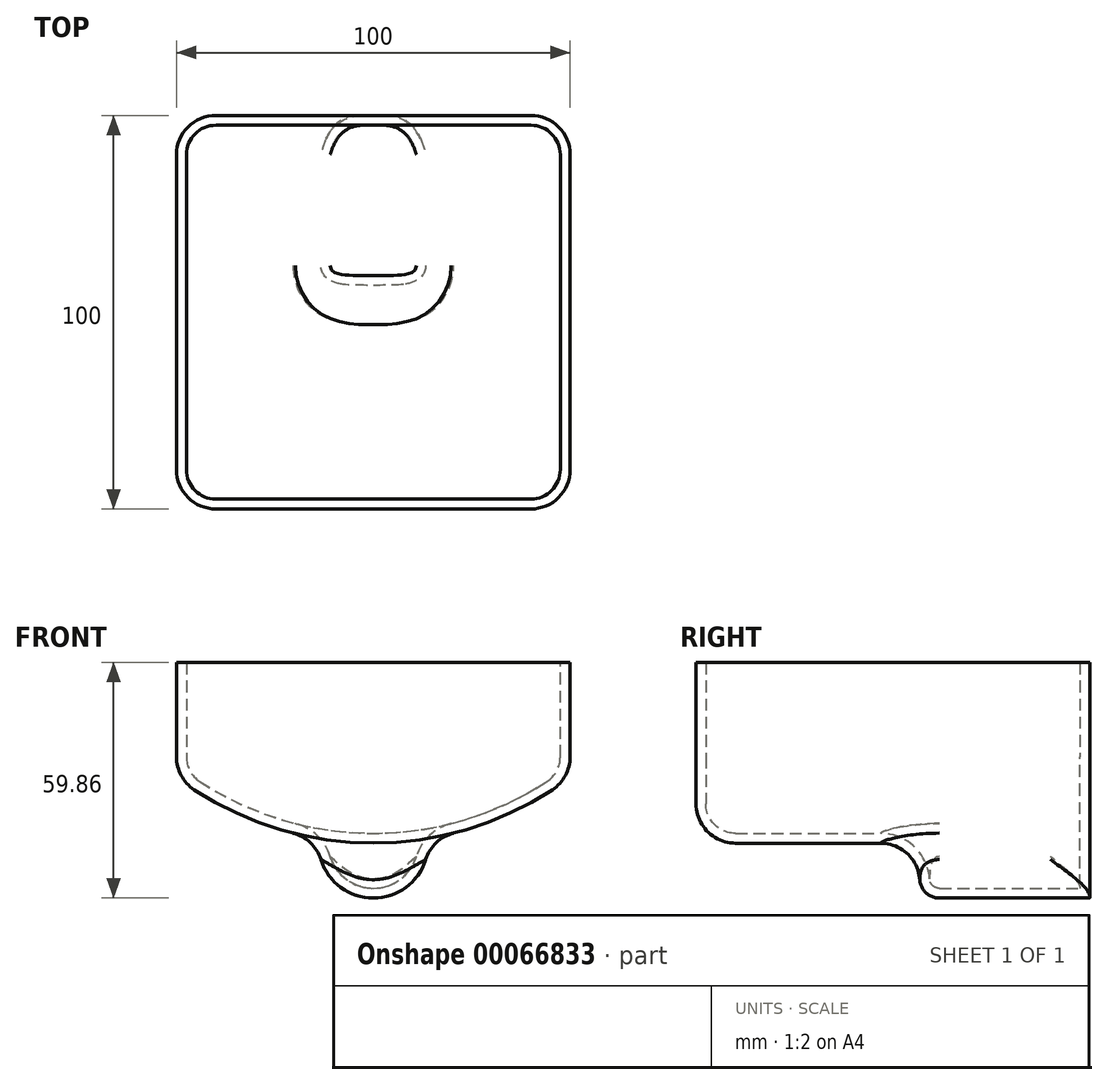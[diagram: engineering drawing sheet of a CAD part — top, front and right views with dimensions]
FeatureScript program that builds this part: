
annotation { "Feature Type Name" : "Feature", "Feature Type Description" : "" }
export const myFeature = defineFeature(function(context is Context, id is Id, definition is map)
    precondition{}
    {
        {
            var Q0;
            Q0=qCreatedBy(makeId("Top.planeOp"),FACE);
            var sketch = newSketch(context, id + "F0", { "sketchPlane" : qUnion([Q0])});
            skLineSegment(sketch, "E0.bottom", {"start": v(-60, -47.01) * mm, "end": v(40, -47.01) * mm});
            skLineSegment(sketch, "E0.top", {"start": v(-60, 52.99) * mm, "end": v(40, 52.99) * mm});
            skLineSegment(sketch, "E0.left", {"start": v(-60, -47.01) * mm, "end": v(-60, 52.99) * mm});
            skLineSegment(sketch, "E0.right", {"start": v(40, -47.01) * mm, "end": v(40, 52.99) * mm});
            skSolve(sketch);
        }
        {
            var Q0;
            Q0=makeQuery(id+"F0.imprint","IMPRINT",FACE,{"disambiguationData":[TD([[makeQuery(id+"F0.imprint","IMPRINT",EDGE,{"derivedFrom":sQuery(id+"F0.wireOp",EDGE,"E0.bottom")}),1.0]])]});
            extrude(context, id + "F1", {"entities" : qUnion([Q0]), "oppositeDirection" : true, "depth" : 50 * mm});
        }
        {
            var Q0;
            Q0=makeQuery(id+"F1.opExtrude","SWEPT_FACE",FACE,{"disambiguationData":[OSD([sQuery(id+"F0.wireOp",EDGE,"E0.top")])]});
            var sketch = newSketch(context, id + "F2", { "sketchPlane" : qUnion([Q0])});
            skArc(sketch, "E1", {"start": v(-40, -29.14) * mm, "mid": v(10, -45.9) * mm, "end": v(60, -29.14) * mm});
            skLineSegment(sketch, "E2", {"start": v(60, -29.14) * mm, "end": v(80.44, -29.14) * mm});
            skLineSegment(sketch, "E3", {"start": v(80.44, -29.14) * mm, "end": v(80.44, -64.36) * mm});
            skLineSegment(sketch, "E4", {"start": v(80.44, -64.36) * mm, "end": v(-57.18, -64.36) * mm});
            skLineSegment(sketch, "E5", {"start": v(-57.18, -64.36) * mm, "end": v(-40, -29.14) * mm});
            skSolve(sketch);
        }
        {
            var Q0;
            Q0 = qSketchRegion(id + "F2", true);
            extrude(context, id + "F3", {"entities" : qUnion([Q0]), "operationType" : NewBodyOperationType.REMOVE, "oppositeDirection" : true, "depth" : 178.14 * mm});
        }
        {
            var Q0;
            Q0=makeQuery(id+"F1.opExtrude","SWEPT_FACE",FACE,{"disambiguationData":[OSD([sQuery(id+"F0.wireOp",EDGE,"E0.top")])]});
            var sketch = newSketch(context, id + "F4", { "sketchPlane" : qUnion([Q0])});
            skCircle(sketch, "E6", {"center": v(10, -45.9) * mm, "radius": 13.95 * mm});
            skSolve(sketch);
        }
        {
            var Q0;
            Q0 = qSketchRegion(id + "F4", true);
            extrude(context, id + "F5", {"entities" : qUnion([Q0]), "operationType" : NewBodyOperationType.ADD, "oppositeDirection" : true, "depth" : 43.18 * mm});
        }
        {
            var Q0;
            Q0=makeQuery(id+"F5.opExtrude","CAP_EDGE",EDGE,{"disambiguationData":[OSD([sQuery(id+"F4.wireOp",EDGE,"E6")])],"isStart":false});
            fillet(context, id + "F6", {"entities" : qUnion([Q0]), "radius" : 5 * mm, "tangentPropagation" : true, "allowEdgeOverflow" : false});
        }
        {
            var Q0;
            Q0=makeQuery(id+"F5.boolean.opBoolean","INTERSECT",EDGE,{"disambiguationData":[OD(0.0)],"derivedFrom":[makeQuery(id+"F3.boolean.opBoolean","COPY",FACE,{"derivedFrom":makeQuery(id+"F3.opExtrude","SWEPT_FACE",FACE,{"disambiguationData":[OSD([sQuery(id+"F2.wireOp",EDGE,"E1")])]})}),makeQuery(id+"F5.opExtrude","SWEPT_FACE",FACE,{"disambiguationData":[OSD([sQuery(id+"F4.wireOp",EDGE,"E6")])]})]});
            var Q1;
            Q1=makeQuery(id+"F1.opExtrude","SWEPT_EDGE",EDGE,{"disambiguationData":[OSD([sQuery(id+"F0.wireOp",EDGE,"E0.top"),sQuery(id+"F0.wireOp",EDGE,"E0.right")])]});
            var Q2;
            Q2=makeQuery(id+"F1.opExtrude","SWEPT_EDGE",EDGE,{"disambiguationData":[OSD([sQuery(id+"F0.wireOp",EDGE,"E0.bottom"),sQuery(id+"F0.wireOp",EDGE,"E0.right")])]});
            var Q3;
            Q3=makeQuery(id+"F1.opExtrude","SWEPT_EDGE",EDGE,{"disambiguationData":[OSD([sQuery(id+"F0.wireOp",EDGE,"E0.top"),sQuery(id+"F0.wireOp",EDGE,"E0.left")])]});
            var Q4;
            Q4=makeQuery(id+"F1.opExtrude","SWEPT_EDGE",EDGE,{"disambiguationData":[OSD([sQuery(id+"F0.wireOp",EDGE,"E0.bottom"),sQuery(id+"F0.wireOp",EDGE,"E0.left")])]});
            var Q5;
            Q5=makeQuery(id+"F3.boolean.opBoolean","COPY",FACE,{"derivedFrom":makeQuery(id+"F3.opExtrude","SWEPT_FACE",FACE,{"disambiguationData":[OSD([sQuery(id+"F2.wireOp",EDGE,"E1")])]})});
            fillet(context, id + "F7", {"entities" : qUnion([Q0, Q1, Q2, Q3, Q4, Q5]), "radius" : 10 * mm, "tangentPropagation" : true, "allowEdgeOverflow" : false});
        }
        {
            var Q0;
            Q0=makeQuery(id+"F1.opExtrude","CAP_FACE",FACE,{"disambiguationData":[OSD([sQuery(id+"F0.wireOp",EDGE,"E0.bottom"),sQuery(id+"F0.wireOp",EDGE,"E0.top"),sQuery(id+"F0.wireOp",EDGE,"E0.left"),sQuery(id+"F0.wireOp",EDGE,"E0.right")])],"isStart":true});
            shell(context, id + "F8", {"entities" : qUnion([Q0]), "thickness" : 2.5 * mm});
        }
    });
